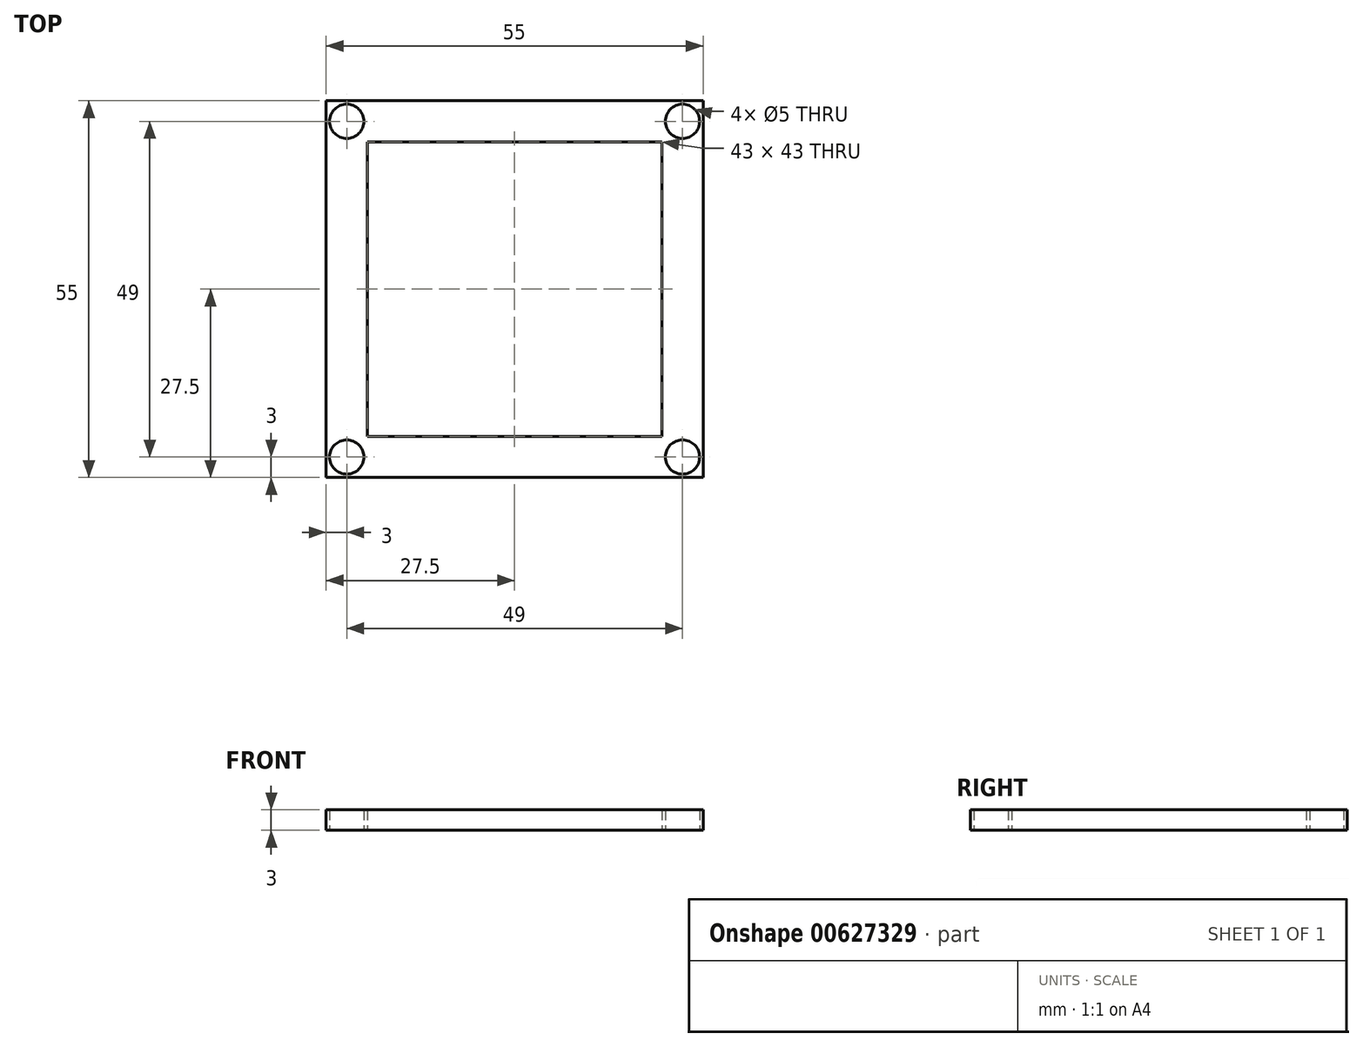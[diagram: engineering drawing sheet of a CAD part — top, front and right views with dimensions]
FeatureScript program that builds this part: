
annotation { "Feature Type Name" : "Feature", "Feature Type Description" : "" }
export const myFeature = defineFeature(function(context is Context, id is Id, definition is map)
    precondition{}
    {
        {
            var Q0;
            Q0=qCreatedBy(makeId("Top.planeOp"),FACE);
            var sketch = newSketch(context, id + "F0", { "sketchPlane" : qUnion([Q0])});
            skLineSegment(sketch, "E0.bottom", {"start": v(27.5, 27.5) * mm, "end": v(-27.5, 27.5) * mm});
            skLineSegment(sketch, "E0.top", {"start": v(27.5, -27.5) * mm, "end": v(-27.5, -27.5) * mm});
            skLineSegment(sketch, "E0.left", {"start": v(27.5, 27.5) * mm, "end": v(27.5, -27.5) * mm});
            skLineSegment(sketch, "E0.right", {"start": v(-27.5, 27.5) * mm, "end": v(-27.5, -27.5) * mm});
            skPoint(sketch, "E0.middle", {"position": v(0, 0) * mm});
            skLineSegment(sketch, "E1.bottom", {"start": v(21.5, 21.5) * mm, "end": v(-21.5, 21.5) * mm});
            skLineSegment(sketch, "E1.top", {"start": v(21.5, -21.5) * mm, "end": v(-21.5, -21.5) * mm});
            skLineSegment(sketch, "E1.left", {"start": v(21.5, 21.5) * mm, "end": v(21.5, -21.5) * mm});
            skLineSegment(sketch, "E1.right", {"start": v(-21.5, 21.5) * mm, "end": v(-21.5, -21.5) * mm});
            skLineSegment(sketch, "E2", {"start": v(-27.5, -27.5) * mm, "end": v(-21.5, -21.5) * mm});
            skLineSegment(sketch, "E3", {"start": v(-21.5, 21.5) * mm, "end": v(-27.5, 27.5) * mm});
            skLineSegment(sketch, "E4", {"start": v(27.5, 27.5) * mm, "end": v(21.5, 21.5) * mm});
            skLineSegment(sketch, "E5", {"start": v(21.5, -21.5) * mm, "end": v(27.5, -27.5) * mm});
            skPoint(sketch, "E6", {"position": v(-24.5, -24.5) * mm});
            skCircle(sketch, "E7", {"center": v(-24.5, -24.5) * mm, "radius": 2.5 * mm});
            skPoint(sketch, "E8", {"position": v(24.5, -24.5) * mm});
            skPoint(sketch, "E9", {"position": v(24.5, 24.5) * mm});
            skPoint(sketch, "E10", {"position": v(-24.5, 24.5) * mm});
            skCircle(sketch, "E11", {"center": v(-24.5, 24.5) * mm, "radius": 2.5 * mm});
            skCircle(sketch, "E12", {"center": v(24.5, -24.5) * mm, "radius": 2.5 * mm});
            skCircle(sketch, "E13", {"center": v(24.5, 24.5) * mm, "radius": 2.5 * mm});
            skSolve(sketch);
        }
        {
            var Q0;
            {var subQ4=sQuery(id+"F0.wireOp",EDGE,"E0.right");Q0=makeQuery(id+"F0.imprint","IMPRINT",FACE,{"disambiguationData":[TD([[makeQuery(id+"F0.imprint","IMPRINT",EDGE,{"derivedFrom":subQ4}),1.0]])]});}
            var Q1;
            {var subQ1=sQuery(id+"F0.wireOp",EDGE,"E0.top");Q1=makeQuery(id+"F0.imprint","IMPRINT",FACE,{"disambiguationData":[TD([[makeQuery(id+"F0.imprint","IMPRINT",EDGE,{"derivedFrom":subQ1}),-1.0]])]});}
            var Q2;
            Q2=makeQuery(id+"F0.imprint","IMPRINT",FACE,{"disambiguationData":[TD([[makeQuery(id+"F0.imprint","IMPRINT",EDGE,{"derivedFrom":sQuery(id+"F0.wireOp",EDGE,"E0.left")}),-1.0]])]});
            var Q3;
            Q3=makeQuery(id+"F0.imprint","IMPRINT",FACE,{"disambiguationData":[TD([[makeQuery(id+"F0.imprint","IMPRINT",EDGE,{"derivedFrom":sQuery(id+"F0.wireOp",EDGE,"E0.bottom")}),1.0]])]});
            extrude(context, id + "F1", {"entities" : qUnion([Q0, Q1, Q2, Q3]), "depth" : 3 * mm, "offsetDistance" : 25 * mm});
        }
    });
